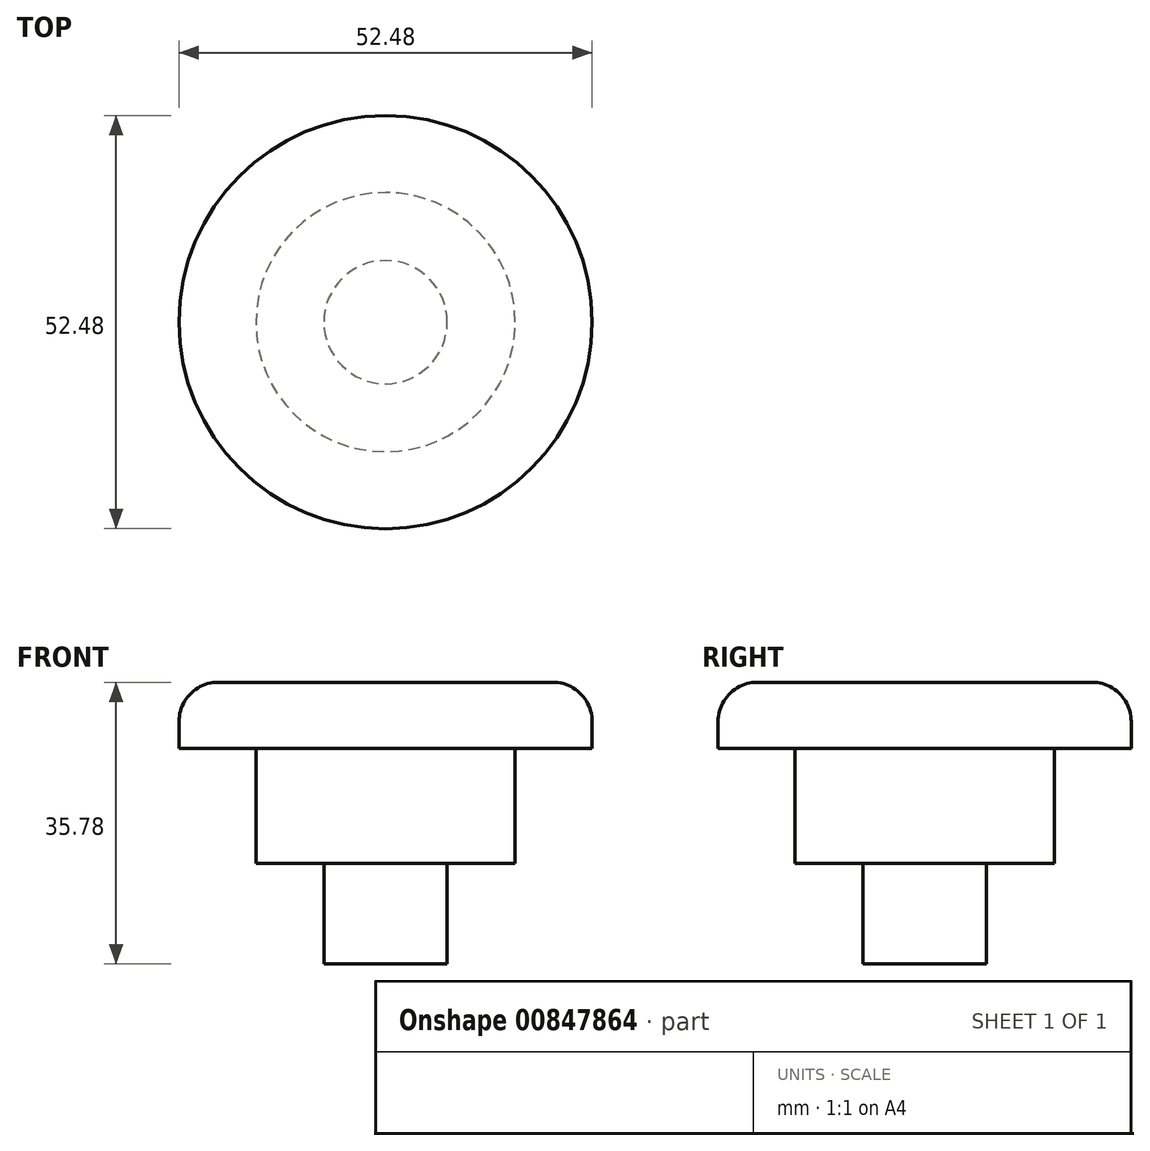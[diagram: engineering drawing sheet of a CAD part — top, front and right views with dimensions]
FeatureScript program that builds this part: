
annotation { "Feature Type Name" : "Feature", "Feature Type Description" : "" }
export const myFeature = defineFeature(function(context is Context, id is Id, definition is map)
    precondition{}
    {
        {
            var Q0;
            Q0=qCreatedBy(makeId("Front.planeOp"),FACE);
            var sketch = newSketch(context, id + "F0", { "sketchPlane" : qUnion([Q0])});
            skLineSegment(sketch, "E0", {"start": v(0, 0) * mm, "end": v(0, -35.78) * mm});
            skLineSegment(sketch, "E1", {"start": v(0, -35.78) * mm, "end": v(7.83, -35.78) * mm});
            skLineSegment(sketch, "E2", {"start": v(7.83, -35.78) * mm, "end": v(7.83, -23.03) * mm});
            skLineSegment(sketch, "E3", {"start": v(7.83, -23.03) * mm, "end": v(16.47, -23.03) * mm});
            skLineSegment(sketch, "E4", {"start": v(16.47, -23.03) * mm, "end": v(16.47, -8.44) * mm});
            skLineSegment(sketch, "E5", {"start": v(16.47, -8.44) * mm, "end": v(26.24, -8.44) * mm});
            skLineSegment(sketch, "E6", {"start": v(26.24, -8.44) * mm, "end": v(26.24, -5) * mm});
            skLineSegment(sketch, "E7", {"start": v(21.24, 0) * mm, "end": v(0, 0) * mm});
            skPoint(sketch, "E8.visualSharp", {"position": v(26.24, 0) * mm});
            skArc(sketch, "E8.filletArc", {"start": v(26.24, -5) * mm, "mid": v(24.78, -1.46) * mm, "end": v(21.24, 0) * mm});
            skSolve(sketch);
        }
        {
            var Q0;
            Q0=makeQuery(id+"F0.imprint","IMPRINT",FACE,{"disambiguationData":[TD([[makeQuery(id+"F0.imprint","IMPRINT",EDGE,{"derivedFrom":sQuery(id+"F0.wireOp",EDGE,"E0")}),1.0]])]});
            var Q1;
            Q1=sQuery(id+"F0.wireOp",EDGE,"E0");
            revolve(context, id + "F1", {"surfaceOperationType" : NewSurfaceOperationType.NEW, "entities" : qUnion([Q0]), "axis" : qUnion([Q1]), "revolveType" : RevolveType.FULL});
        }
    });
